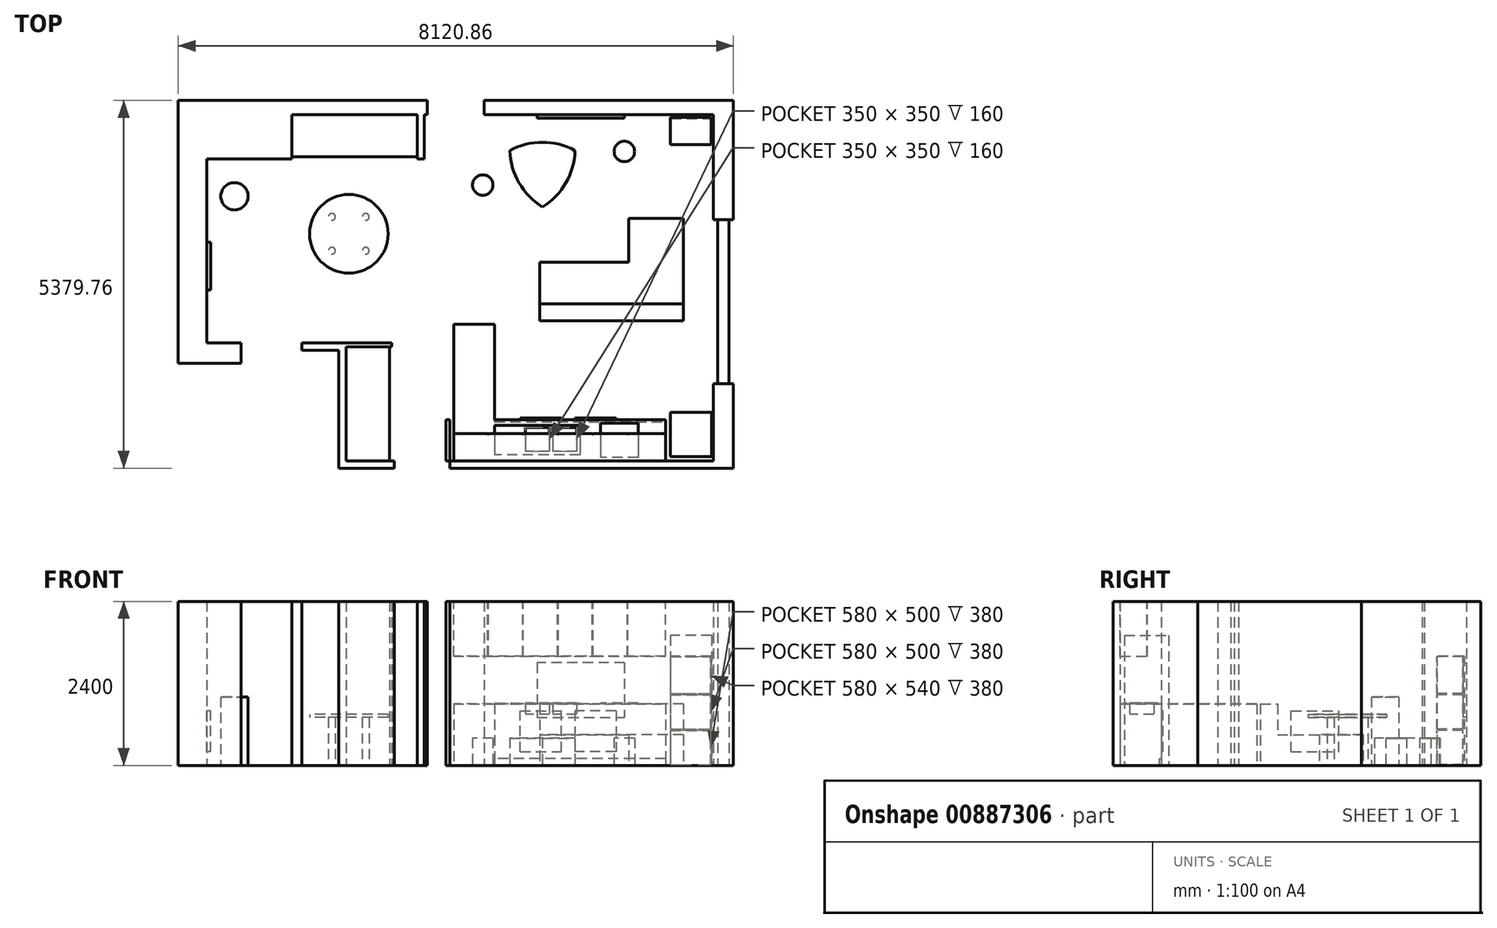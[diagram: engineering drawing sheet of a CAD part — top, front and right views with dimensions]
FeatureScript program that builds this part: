
annotation { "Feature Type Name" : "Feature", "Feature Type Description" : "" }
export const myFeature = defineFeature(function(context is Context, id is Id, definition is map)
    precondition{}
    {
        {
            var Q0;
            Q0=qCreatedBy(makeId("Top.planeOp"),FACE);
            var sketch = newSketch(context, id + "F0", { "sketchPlane" : qUnion([Q0])});
            skLineSegment(sketch, "E0", {"start": v(5332.87, -822.17) * mm, "end": v(1474.75, -822.17) * mm});
            skLineSegment(sketch, "E1", {"start": v(1474.75, -822.17) * mm, "end": v(1474.75, -222.17) * mm});
            skLineSegment(sketch, "E2", {"start": v(1474.75, -222.17) * mm, "end": v(1421.4, -222.17) * mm});
            skLineSegment(sketch, "E3", {"start": v(1421.4, -222.17) * mm, "end": v(1421.4, -822.17) * mm});
            skLineSegment(sketch, "E4", {"start": v(1421.4, -822.17) * mm, "end": v(1474.75, -822.17) * mm});
            skLineSegment(sketch, "E5", {"start": v(5332.87, 309.99) * mm, "end": v(5394.44, 309.99) * mm});
            skLineSegment(sketch, "E6", {"start": v(5394.44, 309.99) * mm, "end": v(5394.44, 2704.75) * mm});
            skLineSegment(sketch, "E7", {"start": v(5394.44, 2704.75) * mm, "end": v(5332.87, 2704.75) * mm});
            skLineSegment(sketch, "E8", {"start": v(5332.87, 2704.75) * mm, "end": v(5332.87, 4243.63) * mm});
            skLineSegment(sketch, "E9", {"start": v(5332.87, 4243.63) * mm, "end": v(1981.19, 4243.63) * mm});
            skLineSegment(sketch, "E10", {"start": v(1981.19, 4243.63) * mm, "end": v(1981.19, 4451) * mm});
            skLineSegment(sketch, "E11", {"start": v(1981.19, 4451) * mm, "end": v(5626.54, 4451) * mm});
            skLineSegment(sketch, "E12", {"start": v(5626.54, 4451) * mm, "end": v(5626.54, 2704.75) * mm});
            skLineSegment(sketch, "E13", {"start": v(5626.54, 2704.75) * mm, "end": v(5394.44, 2704.75) * mm});
            skLineSegment(sketch, "E14", {"start": v(5394.44, 309.99) * mm, "end": v(5626.54, 309.99) * mm});
            skPoint(sketch, "E14.endSnap0", {"position": v(5363.66, 309.99) * mm});
            skLineSegment(sketch, "E15", {"start": v(5626.54, 309.99) * mm, "end": v(5626.54, -928.77) * mm});
            skLineSegment(sketch, "E16", {"start": v(5626.54, -928.77) * mm, "end": v(1474.75, -928.77) * mm});
            skLineSegment(sketch, "E17", {"start": v(1474.75, -928.77) * mm, "end": v(1474.75, -822.17) * mm});
            skLineSegment(sketch, "E18", {"start": v(5558.56, 2704.75) * mm, "end": v(5558.56, 309.99) * mm});
            skLineSegment(sketch, "E19", {"start": v(-37.13, -822.17) * mm, "end": v(664.8, -822.17) * mm});
            skLineSegment(sketch, "E20", {"start": v(664.8, -822.17) * mm, "end": v(664.8, -928.77) * mm});
            skLineSegment(sketch, "E21", {"start": v(664.8, -928.77) * mm, "end": v(-150.57, -928.77) * mm});
            skLineSegment(sketch, "E22", {"start": v(-150.57, -928.77) * mm, "end": v(-150.57, 905.53) * mm});
            skLineSegment(sketch, "E23", {"start": v(-150.57, 905.53) * mm, "end": v(-37.13, 905.53) * mm});
            skLineSegment(sketch, "E24", {"start": v(-37.13, 905.53) * mm, "end": v(-37.13, -26.35) * mm});
            skLineSegment(sketch, "E25", {"start": v(5332.87, 309.99) * mm, "end": v(5332.87, -822.17) * mm});
            skLineSegment(sketch, "E26", {"start": v(-37.13, 905.53) * mm, "end": v(-37.13, -822.17) * mm});
            skLineSegment(sketch, "E27", {"start": v(5332.87, -822.17) * mm, "end": v(1532.87, -822.17) * mm, "construction": true});
            skLineSegment(sketch, "E28", {"start": v(1532.87, -822.17) * mm, "end": v(1532.87, -222.17) * mm});
            skLineSegment(sketch, "E29", {"start": v(1532.87, -222.17) * mm, "end": v(4632.87, -222.17) * mm});
            skLineSegment(sketch, "E30", {"start": v(4894.44, 1227.83) * mm, "end": v(2794.44, 1227.83) * mm});
            skLineSegment(sketch, "E31", {"start": v(2794.44, 1227.83) * mm, "end": v(2794.44, 2087.83) * mm});
            skLineSegment(sketch, "E32", {"start": v(2794.44, 2087.83) * mm, "end": v(4094.44, 2087.83) * mm});
            skLineSegment(sketch, "E33", {"start": v(4894.44, 1227.83) * mm, "end": v(4894.44, 2727.83) * mm});
            skLineSegment(sketch, "E34", {"start": v(4894.44, 2727.83) * mm, "end": v(4094.44, 2727.83) * mm});
            skLineSegment(sketch, "E35", {"start": v(4094.44, 2727.83) * mm, "end": v(4094.44, 2087.83) * mm});
            skLineSegment(sketch, "E36", {"start": v(4894.44, 1227.83) * mm, "end": v(4894.44, 1477.83) * mm, "construction": true});
            skLineSegment(sketch, "E37", {"start": v(4894.44, 1477.83) * mm, "end": v(2794.44, 1477.83) * mm});
            skLineSegment(sketch, "E38.bottom", {"start": v(5301.08, 4208.55) * mm, "end": v(4701.08, 4208.55) * mm});
            skLineSegment(sketch, "E38.top", {"start": v(5301.08, 3808.55) * mm, "end": v(4701.08, 3808.55) * mm});
            skLineSegment(sketch, "E38.left", {"start": v(5301.08, 4208.55) * mm, "end": v(5301.08, 3808.55) * mm});
            skLineSegment(sketch, "E38.right", {"start": v(4701.08, 4208.55) * mm, "end": v(4701.08, 3808.55) * mm});
            skLineSegment(sketch, "E39", {"start": v(4032.87, 4243.63) * mm, "end": v(4032.87, 4193.63) * mm});
            skLineSegment(sketch, "E40", {"start": v(4032.87, 4193.63) * mm, "end": v(2752.87, 4193.63) * mm});
            skLineSegment(sketch, "E41", {"start": v(2752.87, 4193.63) * mm, "end": v(2752.87, 4243.63) * mm});
            skLineSegment(sketch, "E42", {"start": v(2132.87, -302.17) * mm, "end": v(2132.87, -732.17) * mm});
            skLineSegment(sketch, "E43", {"start": v(2132.87, -302.17) * mm, "end": v(3382.87, -302.17) * mm});
            skLineSegment(sketch, "E44", {"start": v(3382.87, -302.17) * mm, "end": v(3382.87, -732.17) * mm});
            skLineSegment(sketch, "E45", {"start": v(3382.87, -732.17) * mm, "end": v(2132.87, -732.17) * mm});
            skLineSegment(sketch, "E46", {"start": v(3382.87, -517.17) * mm, "end": v(3332.87, -517.17) * mm, "construction": true});
            skLineSegment(sketch, "E47", {"start": v(3332.87, -517.17) * mm, "end": v(2982.87, -517.17) * mm, "construction": true});
            skLineSegment(sketch, "E48", {"start": v(2982.87, -517.17) * mm, "end": v(2932.87, -517.17) * mm, "construction": true});
            skLineSegment(sketch, "E49", {"start": v(2932.87, -517.17) * mm, "end": v(2582.87, -517.17) * mm, "construction": true});
            skLineSegment(sketch, "E50.bottom", {"start": v(3332.87, -332.17) * mm, "end": v(2982.87, -332.17) * mm});
            skLineSegment(sketch, "E50.top", {"start": v(3332.87, -682.17) * mm, "end": v(2982.87, -682.17) * mm});
            skLineSegment(sketch, "E50.left", {"start": v(3332.87, -332.17) * mm, "end": v(3332.87, -682.17) * mm});
            skLineSegment(sketch, "E50.right", {"start": v(2982.87, -332.17) * mm, "end": v(2982.87, -682.17) * mm});
            skLineSegment(sketch, "E51.bottom", {"start": v(2932.87, -332.17) * mm, "end": v(2582.87, -332.17) * mm});
            skLineSegment(sketch, "E51.top", {"start": v(2932.87, -682.17) * mm, "end": v(2582.87, -682.17) * mm});
            skLineSegment(sketch, "E51.left", {"start": v(2932.87, -332.17) * mm, "end": v(2932.87, -682.17) * mm});
            skLineSegment(sketch, "E51.right", {"start": v(2582.87, -332.17) * mm, "end": v(2582.87, -682.17) * mm});
            skLineSegment(sketch, "E52.bottom", {"start": v(4232.87, -272.17) * mm, "end": v(3682.87, -272.17) * mm});
            skLineSegment(sketch, "E52.top", {"start": v(4232.87, -772.17) * mm, "end": v(3682.87, -772.17) * mm});
            skLineSegment(sketch, "E52.left", {"start": v(4232.87, -272.17) * mm, "end": v(4232.87, -772.17) * mm});
            skLineSegment(sketch, "E52.right", {"start": v(3682.87, -272.17) * mm, "end": v(3682.87, -772.17) * mm});
            skLineSegment(sketch, "E53", {"start": v(5626.54, 309.99) * mm, "end": v(5626.54, -6920.01) * mm, "construction": true});
            skLineSegment(sketch, "E54", {"start": v(5626.54, -6920.01) * mm, "end": v(109096.54, -6920.01) * mm, "construction": true});
            skLineSegment(sketch, "E55", {"start": v(-150.57, 905.53) * mm, "end": v(-687.76, 905.53) * mm});
            skLineSegment(sketch, "E56", {"start": v(-687.76, 905.53) * mm, "end": v(-687.76, 793.16) * mm});
            skLineSegment(sketch, "E57", {"start": v(-687.76, 793.16) * mm, "end": v(-150.57, 793.16) * mm});
            skLineSegment(sketch, "E58", {"start": v(1145.44, 4243.63) * mm, "end": v(-834.24, 4243.63) * mm});
            skLineSegment(sketch, "E59", {"start": v(-834.24, 4243.63) * mm, "end": v(-834.24, 3594.84) * mm});
            skLineSegment(sketch, "E60", {"start": v(-834.24, 3594.84) * mm, "end": v(-2078.37, 3594.84) * mm});
            skLineSegment(sketch, "E61", {"start": v(-2078.37, 3594.84) * mm, "end": v(-2078.37, 905.53) * mm});
            skLineSegment(sketch, "E62", {"start": v(-2078.37, 905.53) * mm, "end": v(-1579.23, 905.53) * mm});
            skLineSegment(sketch, "E63", {"start": v(-1579.23, 905.53) * mm, "end": v(-1579.23, 605.3) * mm});
            skLineSegment(sketch, "E64", {"start": v(-1579.23, 605.3) * mm, "end": v(-2494.32, 605.3) * mm});
            skLineSegment(sketch, "E65", {"start": v(-2494.32, 605.3) * mm, "end": v(-2494.32, 4451) * mm});
            skLineSegment(sketch, "E66", {"start": v(-2494.32, 4451) * mm, "end": v(1145.44, 4451) * mm});
            skLineSegment(sketch, "E67", {"start": v(1145.44, 4451) * mm, "end": v(1145.44, 4243.63) * mm});
            skLineSegment(sketch, "E68", {"start": v(5332.87, 4243.63) * mm, "end": v(5332.87, 4451) * mm});
            skCircle(sketch, "E69", {"center": v(0, 2500.55) * mm, "radius": 350 * mm, "construction": true});
            skLineSegment(sketch, "E70", {"start": v(-247.49, 2748.03) * mm, "end": v(247.49, 2748.03) * mm, "construction": true});
            skLineSegment(sketch, "E71", {"start": v(247.49, 2748.03) * mm, "end": v(247.49, 2253.06) * mm, "construction": true});
            skLineSegment(sketch, "E72", {"start": v(247.49, 2253.06) * mm, "end": v(-247.49, 2253.06) * mm, "construction": true});
            skCircle(sketch, "E73", {"center": v(-247.49, 2748.03) * mm, "radius": 50 * mm});
            skCircle(sketch, "E74", {"center": v(247.49, 2748.03) * mm, "radius": 50 * mm});
            skCircle(sketch, "E75", {"center": v(247.49, 2253.06) * mm, "radius": 50 * mm});
            skCircle(sketch, "E76", {"center": v(-247.49, 2253.06) * mm, "radius": 50 * mm});
            skCircle(sketch, "E77", {"center": v(0, 2500.55) * mm, "radius": 575 * mm});
            skCircle(sketch, "E78", {"center": v(2832.87, 3443.63) * mm, "radius": 550 * mm, "construction": true});
            skLineSegment(sketch, "E79", {"start": v(2832.87, 3443.63) * mm, "end": v(2832.87, 2893.63) * mm, "construction": true});
            skArc(sketch, "E80", {"start": v(2832.87, 2893.63) * mm, "mid": v(3175.58, 3245.77) * mm, "end": v(3309.19, 3718.63) * mm});
            skArc(sketch, "E81", {"start": v(3309.19, 3718.63) * mm, "mid": v(2832.87, 3839.36) * mm, "end": v(2356.56, 3718.63) * mm});
            skArc(sketch, "E82", {"start": v(2356.56, 3718.63) * mm, "mid": v(2490.17, 3245.77) * mm, "end": v(2832.87, 2893.63) * mm});
            skLineSegment(sketch, "E83", {"start": v(2832.87, 3443.63) * mm, "end": v(3309.19, 3718.63) * mm, "construction": true});
            skLineSegment(sketch, "E84", {"start": v(2832.87, 3443.63) * mm, "end": v(2356.56, 3718.63) * mm, "construction": true});
            skLineSegment(sketch, "E85", {"start": v(3309.19, 3718.63) * mm, "end": v(2356.56, 3718.63) * mm, "construction": true});
            skLineSegment(sketch, "E86", {"start": v(2356.56, 3718.63) * mm, "end": v(2832.87, 2893.63) * mm, "construction": true});
            skLineSegment(sketch, "E87", {"start": v(2832.87, 2893.63) * mm, "end": v(3309.19, 3718.63) * mm, "construction": true});
            skCircle(sketch, "E88", {"center": v(4030.54, 3705.1) * mm, "radius": 150 * mm});
            skCircle(sketch, "E89", {"center": v(1959.1, 3213.96) * mm, "radius": 150 * mm});
            skLineSegment(sketch, "E90", {"start": v(1101.26, 4243.63) * mm, "end": v(1101.26, 3594.84) * mm});
            skLineSegment(sketch, "E91", {"start": v(1101.26, 3594.84) * mm, "end": v(1001.26, 3594.84) * mm});
            skLineSegment(sketch, "E92", {"start": v(1001.26, 3594.84) * mm, "end": v(1001.26, 4243.63) * mm});
            skLineSegment(sketch, "E93", {"start": v(1001.26, 3627.05) * mm, "end": v(-834.24, 3627.05) * mm});
            skLineSegment(sketch, "E94", {"start": v(597.97, -822.17) * mm, "end": v(597.97, 845.53) * mm});
            skLineSegment(sketch, "E95", {"start": v(597.97, 905.53) * mm, "end": v(624.1, 905.53) * mm});
            skLineSegment(sketch, "E96", {"start": v(624.1, 905.53) * mm, "end": v(624.1, 845.53) * mm});
            skLineSegment(sketch, "E97", {"start": v(624.1, 845.53) * mm, "end": v(-37.13, 845.53) * mm});
            skLineSegment(sketch, "E98", {"start": v(-37.13, 905.53) * mm, "end": v(597.97, 905.53) * mm});
            skCircle(sketch, "E99", {"center": v(-1673.98, 3049.9) * mm, "radius": 200 * mm});
            skLineSegment(sketch, "E100", {"start": v(1532.87, -222.17) * mm, "end": v(1532.87, 1177.83) * mm});
            skLineSegment(sketch, "E101", {"start": v(1532.87, 1177.83) * mm, "end": v(2132.87, 1177.83) * mm});
            skLineSegment(sketch, "E102", {"start": v(2132.87, 1177.83) * mm, "end": v(2132.87, -222.17) * mm});
            skLineSegment(sketch, "E103", {"start": v(4632.87, -222.17) * mm, "end": v(4632.87, -822.17) * mm});
            skLineSegment(sketch, "E104.bottom", {"start": v(5306, -761.63) * mm, "end": v(4706, -761.63) * mm});
            skLineSegment(sketch, "E104.top", {"start": v(5306, -111.63) * mm, "end": v(4706, -111.63) * mm});
            skLineSegment(sketch, "E104.left", {"start": v(5306, -761.63) * mm, "end": v(5306, -111.63) * mm});
            skLineSegment(sketch, "E104.right", {"start": v(4706, -761.63) * mm, "end": v(4706, -111.63) * mm});
            skSolve(sketch);
        }
        {
            var Q0;
            {var subQ0=sQuery(id+"F0.wireOp",EDGE,"E7");Q0=makeQuery(id+"F0.imprint","IMPRINT",FACE,{"disambiguationData":[TD([[makeQuery(id+"F0.imprint","IMPRINT",EDGE,{"derivedFrom":subQ0}),-1.0]])]});}
            var Q1;
            Q1=makeQuery(id+"F0.imprint","IMPRINT",FACE,{"disambiguationData":[TD([[makeQuery(id+"F0.imprint","IMPRINT",EDGE,{"derivedFrom":sQuery(id+"F0.wireOp",EDGE,"E0")}),1.0]])]});
            var Q2;
            {var subQ0=sQuery(id+"F0.wireOp",EDGE,"E19");Q2=makeQuery(id+"F0.imprint","IMPRINT",FACE,{"disambiguationData":[TD([[makeQuery(id+"F0.imprint","IMPRINT",EDGE,{"derivedFrom":subQ0}),-1.0]])]});}
            var Q3;
            Q3=makeQuery(id+"F0.imprint","IMPRINT",FACE,{"disambiguationData":[TD([[makeQuery(id+"F0.imprint","IMPRINT",EDGE,{"derivedFrom":sQuery(id+"F0.wireOp",EDGE,"E1")}),1.0]])]});
            var Q4;
            Q4=makeQuery(id+"F0.imprint","IMPRINT",FACE,{"disambiguationData":[TD([[makeQuery(id+"F0.imprint","IMPRINT",EDGE,{"derivedFrom":sQuery(id+"F0.wireOp",EDGE,"E58")}),-1.0]])]});
            var Q5;
            {var subQ0=sQuery(id+"F0.wireOp",EDGE,"E55");Q5=makeQuery(id+"F0.imprint","IMPRINT",FACE,{"disambiguationData":[TD([[makeQuery(id+"F0.imprint","IMPRINT",EDGE,{"derivedFrom":subQ0}),1.0]])]});}
            var Q6;
            {var subQ0=sQuery(id+"F0.wireOp",EDGE,"E10");Q6=makeQuery(id+"F0.imprint","IMPRINT",FACE,{"disambiguationData":[TD([[makeQuery(id+"F0.imprint","IMPRINT",EDGE,{"derivedFrom":subQ0}),-1.0]])]});}
            var Q7;
            {var subQ3=sQuery(id+"F0.wireOp",EDGE,"E90");Q7=makeQuery(id+"F0.imprint","IMPRINT",FACE,{"disambiguationData":[TD([[makeQuery(id+"F0.imprint","IMPRINT",EDGE,{"derivedFrom":subQ3}),-1.0]])]});}
            var Q8;
            Q8=makeQuery(id+"F0.imprint","IMPRINT",FACE,{"disambiguationData":[TD([[makeQuery(id+"F0.imprint","IMPRINT",EDGE,{"derivedFrom":sQuery(id+"F0.wireOp",EDGE,"E95")}),-1.0]])]});
            extrude(context, id + "F1", {"entities" : qUnion([Q0, Q1, Q2, Q3, Q4, Q5, Q6, Q7, Q8]), "depth" : 2400 * mm, "offsetDistance" : 25 * mm});
        }
        {
            var Q0;
            {var subQ1=sQuery(id+"F0.wireOp",EDGE,"E28");Q0=makeQuery(id+"F0.imprint","IMPRINT",FACE,{"disambiguationData":[TD([[makeQuery(id+"F0.imprint","IMPRINT",EDGE,{"derivedFrom":subQ1}),-1.0]])]});}
            var Q1;
            {var subQ0=sQuery(id+"F0.wireOp",EDGE,"E100");Q1=makeQuery(id+"F0.imprint","IMPRINT",FACE,{"disambiguationData":[TD([[makeQuery(id+"F0.imprint","IMPRINT",EDGE,{"derivedFrom":subQ0}),-1.0]])]});}
            extrude(context, id + "F2", {"entities" : qUnion([Q0, Q1]), "depth" : 900 * mm, "offsetDistance" : 25 * mm});
        }
        {
            var Q0;
            Q0=makeQuery(id+"F1.opExtrude","CAP_FACE",FACE,{"disambiguationData":[OSD([sQuery(id+"F0.wireOp",EDGE,"E0"),sQuery(id+"F0.wireOp",EDGE,"E5"),sQuery(id+"F0.wireOp",EDGE,"E14"),sQuery(id+"F0.wireOp",EDGE,"E15"),sQuery(id+"F0.wireOp",EDGE,"E16"),sQuery(id+"F0.wireOp",EDGE,"E17"),sQuery(id+"F0.wireOp",EDGE,"E25")])],"isStart":false});
            var sketch = newSketch(context, id + "F3", { "sketchPlane" : qUnion([Q0])});
            skLineSegment(sketch, "E105", {"start": v(4632.87, -822.17) * mm, "end": v(1532.87, -822.17) * mm});
            skLineSegment(sketch, "E106", {"start": v(1532.87, -822.17) * mm, "end": v(1532.87, -422.17) * mm});
            skLineSegment(sketch, "E107", {"start": v(1532.87, -422.17) * mm, "end": v(4632.87, -422.17) * mm});
            skLineSegment(sketch, "E108", {"start": v(4632.87, -822.17) * mm, "end": v(4632.87, -422.17) * mm});
            skSolve(sketch);
        }
        {
            var Q0;
            Q0=makeQuery(id+"F3.imprint","IMPRINT",FACE,{"disambiguationData":[TD([[makeQuery(id+"F3.imprint","IMPRINT",EDGE,{"derivedFrom":sQuery(id+"F3.wireOp",EDGE,"E105")}),-1.0]])]});
            extrude(context, id + "F4", {"entities" : qUnion([Q0]), "oppositeDirection" : true, "depth" : 800 * mm, "offsetDistance" : 25 * mm});
        }
        {
            var Q0;
            Q0=makeQuery(id+"F0.imprint","IMPRINT",FACE,{"disambiguationData":[TD([[makeQuery(id+"F0.imprint","IMPRINT",EDGE,{"derivedFrom":sQuery(id+"F0.wireOp",EDGE,"nRFYV91U-GxAd-OucP-NhtY-qvlqKsGYWcc8.bottom")}),1.0]])]});
            var Q1;
            Q1=makeQuery(id+"F0.imprint","IMPRINT",FACE,{"disambiguationData":[TD([[makeQuery(id+"F0.imprint","IMPRINT",EDGE,{"derivedFrom":sQuery(id+"F0.wireOp",EDGE,"E104.bottom")}),-1.0]])]});
            extrude(context, id + "F5", {"entities" : qUnion([Q0, Q1]), "depth" : 1900 * mm, "offsetDistance" : 25 * mm});
        }
        {
            var Q0;
            {var subQ0=sQuery(id+"F0.wireOp",EDGE,"E30");Q0=makeQuery(id+"F0.imprint","IMPRINT",FACE,{"disambiguationData":[TD([[makeQuery(id+"F0.imprint","IMPRINT",EDGE,{"derivedFrom":subQ0}),-1.0]])]});}
            extrude(context, id + "F6", {"entities" : qUnion([Q0]), "depth" : 900 * mm, "offsetDistance" : 25 * mm});
        }
        {
            var Q0;
            {var subQ3=sQuery(id+"F0.wireOp",EDGE,"E32");Q0=makeQuery(id+"F0.imprint","IMPRINT",FACE,{"disambiguationData":[TD([[makeQuery(id+"F0.imprint","IMPRINT",EDGE,{"derivedFrom":subQ3}),-1.0]])]});}
            extrude(context, id + "F7", {"entities" : qUnion([Q0]), "operationType" : NewBodyOperationType.ADD, "depth" : 450 * mm, "offsetDistance" : 25 * mm});
        }
        {
            var Q0;
            Q0=makeQuery(id+"F0.imprint","IMPRINT",FACE,{"disambiguationData":[TD([[makeQuery(id+"F0.imprint","IMPRINT",EDGE,{"derivedFrom":sQuery(id+"F0.wireOp",EDGE,"E42")}),1.0]])]});
            extrude(context, id + "F8", {"entities" : qUnion([Q0]), "operationType" : NewBodyOperationType.ADD, "depth" : 910 * mm, "offsetDistance" : 25 * mm});
        }
        {
            var Q0;
            Q0=makeQuery(id+"F0.imprint","IMPRINT",FACE,{"disambiguationData":[TD([[makeQuery(id+"F0.imprint","IMPRINT",EDGE,{"derivedFrom":sQuery(id+"F0.wireOp",EDGE,"E50.bottom")}),1.0]])]});
            var Q1;
            Q1=makeQuery(id+"F0.imprint","IMPRINT",FACE,{"disambiguationData":[TD([[makeQuery(id+"F0.imprint","IMPRINT",EDGE,{"derivedFrom":sQuery(id+"F0.wireOp",EDGE,"E51.bottom")}),1.0]])]});
            extrude(context, id + "F9", {"entities" : qUnion([Q0, Q1]), "operationType" : NewBodyOperationType.ADD, "depth" : 750 * mm, "offsetDistance" : 25 * mm});
        }
        {
            var Q0;
            Q0=makeQuery(id+"F0.imprint","IMPRINT",FACE,{"disambiguationData":[TD([[makeQuery(id+"F0.imprint","IMPRINT",EDGE,{"derivedFrom":sQuery(id+"F0.wireOp",EDGE,"E52.bottom")}),1.0]])]});
            extrude(context, id + "F10", {"entities" : qUnion([Q0]), "operationType" : NewBodyOperationType.ADD, "depth" : 910 * mm, "offsetDistance" : 25 * mm});
        }
        {
            var Q0;
            {var subQ0=sQuery(id+"F0.wireOp",EDGE,"E6");Q0=makeQuery(id+"F0.imprint","IMPRINT",FACE,{"disambiguationData":[TD([[makeQuery(id+"F0.imprint","IMPRINT",EDGE,{"derivedFrom":subQ0}),-1.0]])]});}
            extrude(context, id + "F11", {"entities" : qUnion([Q0]), "depth" : 2400 * mm, "offsetDistance" : 25 * mm});
        }
        {
            var Q0;
            Q0=makeQuery(id+"F0.imprint","IMPRINT",FACE,{"disambiguationData":[TD([[makeQuery(id+"F0.imprint","IMPRINT",EDGE,{"derivedFrom":sQuery(id+"F0.wireOp",EDGE,"E73")}),-1.0]])]});
            var Q1;
            Q1=makeQuery(id+"Fm7Inrb7nq87sZd_8.opExtrude","CAP_FACE",FACE,{"disambiguationData":[OSD([sQuery(id+"F0.wireOp",EDGE,"E74")])],"isStart":false});
            var Q2;
            Q2=makeQuery(id+"Fm7Inrb7nq87sZd_8.opExtrude","CAP_FACE",FACE,{"disambiguationData":[OSD([sQuery(id+"F0.wireOp",EDGE,"E75")])],"isStart":false});
            var Q3;
            Q3=makeQuery(id+"Fm7Inrb7nq87sZd_8.opExtrude","CAP_FACE",FACE,{"disambiguationData":[OSD([sQuery(id+"F0.wireOp",EDGE,"E73")])],"isStart":false});
            var Q4;
            Q4=makeQuery(id+"Fm7Inrb7nq87sZd_8.opExtrude","CAP_FACE",FACE,{"disambiguationData":[OSD([sQuery(id+"F0.wireOp",EDGE,"E76")])],"isStart":false});
            var Q5;
            Q5=makeQuery(id+"F0.imprint","IMPRINT",FACE,{"disambiguationData":[TD([[makeQuery(id+"F0.imprint","IMPRINT",EDGE,{"derivedFrom":sQuery(id+"F0.wireOp",EDGE,"E74")}),1.0]])]});
            var Q6;
            Q6=makeQuery(id+"F0.imprint","IMPRINT",FACE,{"disambiguationData":[TD([[makeQuery(id+"F0.imprint","IMPRINT",EDGE,{"derivedFrom":sQuery(id+"F0.wireOp",EDGE,"E75")}),1.0]])]});
            var Q7;
            Q7=makeQuery(id+"F0.imprint","IMPRINT",FACE,{"disambiguationData":[TD([[makeQuery(id+"F0.imprint","IMPRINT",EDGE,{"derivedFrom":sQuery(id+"F0.wireOp",EDGE,"E73")}),1.0]])]});
            var Q8;
            Q8=makeQuery(id+"F0.imprint","IMPRINT",FACE,{"disambiguationData":[TD([[makeQuery(id+"F0.imprint","IMPRINT",EDGE,{"derivedFrom":sQuery(id+"F0.wireOp",EDGE,"E76")}),1.0]])]});
            extrude(context, id + "F12", {"entities" : qUnion([Q0, Q1, Q2, Q3, Q4, Q5, Q6, Q7, Q8]), "depth" : 750 * mm, "offsetDistance" : 25 * mm});
        }
        {
            var Q0;
            Q0=makeQuery(id+"F0.imprint","IMPRINT",FACE,{"disambiguationData":[TD([[makeQuery(id+"F0.imprint","IMPRINT",EDGE,{"derivedFrom":sQuery(id+"F0.wireOp",EDGE,"E73")}),-1.0]])]});
            extrude(context, id + "F13", {"entities" : qUnion([Q0]), "depth" : 700 * mm, "offsetDistance" : 25 * mm});
        }
        {
            var Q0;
            Q0=makeQuery(id+"F13.opExtrude","SWEPT_BODY",BODY,{"disambiguationData":[OSD([sQuery(id+"F0.wireOp",EDGE,"E73"),sQuery(id+"F0.wireOp",EDGE,"E74"),sQuery(id+"F0.wireOp",EDGE,"E75"),sQuery(id+"F0.wireOp",EDGE,"E76"),sQuery(id+"F0.wireOp",EDGE,"E77")])]});
            var Q1;
            Q1=makeQuery(id+"F12.opExtrude","SWEPT_BODY",BODY,{"disambiguationData":[OSD([sQuery(id+"F0.wireOp",EDGE,"E73"),sQuery(id+"F0.wireOp",EDGE,"E74"),sQuery(id+"F0.wireOp",EDGE,"E75"),sQuery(id+"F0.wireOp",EDGE,"E76"),sQuery(id+"F0.wireOp",EDGE,"E77")])]});
            booleanBodies(context, id + "F14", {"operationType" : BooleanOperationType.SUBTRACTION, "tools" : qUnion([Q0]), "targets" : qUnion([Q1])});
        }
        {
            var Q0;
            {var subQ0=sQuery(id+"F0.wireOp",EDGE,"E39");Q0=makeQuery(id+"F0.imprint","IMPRINT",FACE,{"disambiguationData":[TD([[makeQuery(id+"F0.imprint","IMPRINT",EDGE,{"derivedFrom":subQ0}),-1.0]])]});}
            extrude(context, id + "F15", {"entities" : qUnion([Q0]), "depth" : 1500 * mm, "offsetDistance" : 25 * mm});
        }
        {
            var Q0;
            Q0=makeQuery(id+"F15.opExtrude","SWEPT_FACE",FACE,{"disambiguationData":[OSD([sQuery(id+"F0.wireOp",EDGE,"E40")])]});
            var sketch = newSketch(context, id + "F16", { "sketchPlane" : qUnion([Q0])});
            skLineSegment(sketch, "E109.bottom", {"start": v(2752.87, 0) * mm, "end": v(4032.87, 0) * mm});
            skLineSegment(sketch, "E109.top", {"start": v(2752.87, 700) * mm, "end": v(4032.87, 700) * mm});
            skLineSegment(sketch, "E109.left", {"start": v(2752.87, 0) * mm, "end": v(2752.87, 700) * mm});
            skLineSegment(sketch, "E109.right", {"start": v(4032.87, 0) * mm, "end": v(4032.87, 700) * mm});
            skSolve(sketch);
        }
        {
            var Q0;
            Q0=makeQuery(id+"F16.imprint","IMPRINT",FACE,{"disambiguationData":[TD([[makeQuery(id+"F16.imprint","IMPRINT",EDGE,{"derivedFrom":sQuery(id+"F16.wireOp",EDGE,"E109.bottom")}),-1.0]])]});
            extrude(context, id + "F17", {"entities" : qUnion([Q0]), "operationType" : NewBodyOperationType.REMOVE, "oppositeDirection" : true, "depth" : 50 * mm, "offsetDistance" : 25 * mm});
        }
        {
            var Q0;
            Q0=makeQuery(id+"F0.imprint","IMPRINT",FACE,{"disambiguationData":[TD([[makeQuery(id+"F0.imprint","IMPRINT",EDGE,{"derivedFrom":sQuery(id+"F0.wireOp",EDGE,"E80")}),1.0]])]});
            var Q1;
            Q1=makeQuery(id+"F0.imprint","IMPRINT",FACE,{"disambiguationData":[TD([[makeQuery(id+"F0.imprint","IMPRINT",EDGE,{"derivedFrom":sQuery(id+"F0.wireOp",EDGE,"E88")}),1.0]])]});
            var Q2;
            Q2=makeQuery(id+"F0.imprint","IMPRINT",FACE,{"disambiguationData":[TD([[makeQuery(id+"F0.imprint","IMPRINT",EDGE,{"derivedFrom":sQuery(id+"F0.wireOp",EDGE,"E89")}),1.0]])]});
            extrude(context, id + "F18", {"entities" : qUnion([Q0, Q1, Q2]), "depth" : 400 * mm, "offsetDistance" : 25 * mm});
        }
        {
            var Q0;
            Q0=makeQuery(id+"F0.imprint","IMPRINT",FACE,{"disambiguationData":[TD([[makeQuery(id+"F0.imprint","IMPRINT",EDGE,{"derivedFrom":sQuery(id+"F0.wireOp",EDGE,"E38.bottom")}),1.0]])]});
            extrude(context, id + "F19", {"entities" : qUnion([Q0]), "depth" : 1600 * mm, "offsetDistance" : 25 * mm});
        }
        {
            var Q0;
            Q0=makeQuery(id+"F19.opExtrude","SWEPT_FACE",FACE,{"disambiguationData":[OSD([sQuery(id+"F0.wireOp",EDGE,"E38.top")])]});
            var sketch = newSketch(context, id + "F20", { "sketchPlane" : qUnion([Q0])});
            skCircle(sketch, "E110", {"center": v(4701.08, 1600) * mm, "radius": 10 * mm, "construction": true});
            skCircle(sketch, "E111", {"center": v(5301.08, 1600) * mm, "radius": 10 * mm, "construction": true});
            skLineSegment(sketch, "E112", {"start": v(4701.08, 1590) * mm, "end": v(5301.08, 1590) * mm, "construction": true});
            skCircle(sketch, "E113", {"center": v(4701.08, 0) * mm, "radius": 10 * mm, "construction": true});
            skCircle(sketch, "E114", {"center": v(5301.08, 0) * mm, "radius": 10 * mm, "construction": true});
            skLineSegment(sketch, "E115", {"start": v(5301.08, 10) * mm, "end": v(4701.08, 10) * mm, "construction": true});
            skLineSegment(sketch, "E116", {"start": v(4711.08, 0) * mm, "end": v(4711.08, 10) * mm, "construction": true});
            skLineSegment(sketch, "E117", {"start": v(5291.08, 0) * mm, "end": v(5291.08, 10) * mm, "construction": true});
            skLineSegment(sketch, "E118", {"start": v(4711.08, 1600) * mm, "end": v(4711.08, 1590) * mm, "construction": true});
            skLineSegment(sketch, "E119.bottom", {"start": v(4711.08, 1590) * mm, "end": v(5291.08, 1590) * mm, "construction": true});
            skLineSegment(sketch, "E119.top", {"start": v(4711.08, 10) * mm, "end": v(5291.08, 10) * mm, "construction": true});
            skLineSegment(sketch, "E119.left", {"start": v(4711.08, 1590) * mm, "end": v(4711.08, 10) * mm, "construction": true});
            skLineSegment(sketch, "E119.right", {"start": v(5291.08, 1590) * mm, "end": v(5291.08, 10) * mm, "construction": true});
            skLineSegment(sketch, "E120.bottom", {"start": v(4711.08, 10) * mm, "end": v(5291.08, 10) * mm});
            skLineSegment(sketch, "E120.top", {"start": v(4711.08, 510) * mm, "end": v(5291.08, 510) * mm});
            skLineSegment(sketch, "E120.left", {"start": v(4711.08, 10) * mm, "end": v(4711.08, 510) * mm});
            skLineSegment(sketch, "E120.right", {"start": v(5291.08, 10) * mm, "end": v(5291.08, 510) * mm});
            skLineSegment(sketch, "E121", {"start": v(4711.08, 510) * mm, "end": v(4711.08, 530) * mm, "construction": true});
            skLineSegment(sketch, "E122.bottom", {"start": v(4711.08, 530) * mm, "end": v(5291.08, 530) * mm});
            skLineSegment(sketch, "E122.top", {"start": v(4711.08, 1030) * mm, "end": v(5291.08, 1030) * mm});
            skLineSegment(sketch, "E122.left", {"start": v(4711.08, 530) * mm, "end": v(4711.08, 1030) * mm});
            skLineSegment(sketch, "E122.right", {"start": v(5291.08, 530) * mm, "end": v(5291.08, 1030) * mm});
            skLineSegment(sketch, "E123", {"start": v(4711.08, 1030) * mm, "end": v(4711.08, 1050) * mm, "construction": true});
            skLineSegment(sketch, "E124.bottom", {"start": v(4711.08, 1050) * mm, "end": v(5291.08, 1050) * mm});
            skLineSegment(sketch, "E124.top", {"start": v(4711.08, 1590) * mm, "end": v(5291.08, 1590) * mm});
            skLineSegment(sketch, "E124.left", {"start": v(4711.08, 1050) * mm, "end": v(4711.08, 1590) * mm});
            skLineSegment(sketch, "E124.right", {"start": v(5291.08, 1050) * mm, "end": v(5291.08, 1590) * mm});
            skSolve(sketch);
        }
        {
            var Q0;
            Q0=makeQuery(id+"F20.imprint","IMPRINT",FACE,{"disambiguationData":[TD([[makeQuery(id+"F20.imprint","IMPRINT",EDGE,{"derivedFrom":sQuery(id+"F20.wireOp",EDGE,"E124.bottom")}),1.0]])]});
            var Q1;
            Q1=makeQuery(id+"F20.imprint","IMPRINT",FACE,{"disambiguationData":[TD([[makeQuery(id+"F20.imprint","IMPRINT",EDGE,{"derivedFrom":sQuery(id+"F20.wireOp",EDGE,"E122.bottom")}),1.0]])]});
            var Q2;
            Q2=makeQuery(id+"F20.imprint","IMPRINT",FACE,{"disambiguationData":[TD([[makeQuery(id+"F20.imprint","IMPRINT",EDGE,{"derivedFrom":sQuery(id+"F20.wireOp",EDGE,"E120.bottom")}),1.0]])]});
            extrude(context, id + "F21", {"entities" : qUnion([Q0, Q1, Q2]), "operationType" : NewBodyOperationType.REMOVE, "oppositeDirection" : true, "depth" : 380 * mm, "offsetDistance" : 25 * mm});
        }
        {
            var Q0;
            Q0=makeQuery(id+"F2.opExtrude","SWEPT_FACE",FACE,{"disambiguationData":[OSD([sQuery(id+"F0.wireOp",EDGE,"E29")])]});
            var sketch = newSketch(context, id + "F22", { "sketchPlane" : qUnion([Q0])});
            skLineSegment(sketch, "E125", {"start": v(-4632.87, 100) * mm, "end": v(-4632.87, 100) * mm});
            skLineSegment(sketch, "E126.bottom", {"start": v(-2507.98, 200) * mm, "end": v(-3107.98, 200) * mm});
            skLineSegment(sketch, "E126.top", {"start": v(-2507.98, 800) * mm, "end": v(-3107.98, 800) * mm});
            skLineSegment(sketch, "E126.left", {"start": v(-2507.98, 200) * mm, "end": v(-2507.98, 800) * mm});
            skLineSegment(sketch, "E126.right", {"start": v(-3107.98, 200) * mm, "end": v(-3107.98, 800) * mm});
            skLineSegment(sketch, "E127", {"start": v(-1532.87, 900) * mm, "end": v(-1532.87, 0) * mm, "construction": true});
            skLineSegment(sketch, "E128", {"start": v(-4632.87, 900) * mm, "end": v(-4632.87, 0) * mm, "construction": true});
            skLineSegment(sketch, "E129.bottom", {"start": v(-3907.98, 800) * mm, "end": v(-3307.98, 800) * mm});
            skLineSegment(sketch, "E129.top", {"start": v(-3907.98, 200) * mm, "end": v(-3307.98, 200) * mm});
            skLineSegment(sketch, "E129.left", {"start": v(-3907.98, 800) * mm, "end": v(-3907.98, 200) * mm});
            skLineSegment(sketch, "E129.right", {"start": v(-3307.98, 800) * mm, "end": v(-3307.98, 200) * mm});
            skLineSegment(sketch, "E130", {"start": v(-4632.87, 100) * mm, "end": v(-2132.87, 100) * mm});
            skSolve(sketch);
        }
        {
            var Q0;
            Q0=makeQuery(id+"F22.imprint","IMPRINT",FACE,{"disambiguationData":[TD([[makeQuery(id+"F22.imprint","IMPRINT",EDGE,{"derivedFrom":sQuery(id+"F22.wireOp",EDGE,"E129.bottom")}),-1.0]])]});
            var Q1;
            Q1=makeQuery(id+"F22.imprint","IMPRINT",FACE,{"disambiguationData":[TD([[makeQuery(id+"F22.imprint","IMPRINT",EDGE,{"derivedFrom":sQuery(id+"F22.wireOp",EDGE,"E126.bottom")}),-1.0]])]});
            extrude(context, id + "F23", {"entities" : qUnion([Q0, Q1]), "operationType" : NewBodyOperationType.ADD, "depth" : 25 * mm, "offsetDistance" : 25 * mm});
        }
        {
            var Q0;
            {var subQ0=sQuery(id+"F22.wireOp",EDGE,"E130");Q0=makeQuery(id+"F22.imprint","IMPRINT",FACE,{"disambiguationData":[TD([[makeQuery(id+"F22.imprint","IMPRINT",EDGE,{"derivedFrom":subQ0}),-1.0]])]});}
            extrude(context, id + "F24", {"entities" : qUnion([Q0]), "operationType" : NewBodyOperationType.REMOVE, "oppositeDirection" : true, "depth" : 30 * mm, "offsetDistance" : 25 * mm});
        }
        {
            var Q0;
            Q0=makeQuery(id+"F4.opExtrude","SWEPT_FACE",FACE,{"disambiguationData":[OSD([sQuery(id+"F3.wireOp",EDGE,"E107")])]});
            var sketch = newSketch(context, id + "F25", { "sketchPlane" : qUnion([Q0])});
            skLineSegment(sketch, "E131", {"start": v(-1532.87, 1600) * mm, "end": v(-1532.87, 2400) * mm, "construction": true});
            skLineSegment(sketch, "E132", {"start": v(-1532.87, 1600) * mm, "end": v(-2032.87, 1600) * mm, "construction": true});
            skLineSegment(sketch, "E133.bottom", {"start": v(-2032.87, 1600) * mm, "end": v(-2042.87, 1600) * mm});
            skLineSegment(sketch, "E133.top", {"start": v(-2032.87, 2400) * mm, "end": v(-2042.87, 2400) * mm});
            skLineSegment(sketch, "E133.left", {"start": v(-2032.87, 1600) * mm, "end": v(-2032.87, 2400) * mm});
            skLineSegment(sketch, "E133.right", {"start": v(-2042.87, 1600) * mm, "end": v(-2042.87, 2400) * mm});
            skLineSegment(sketch, "E134", {"start": v(-2042.87, 1600) * mm, "end": v(-2542.87, 1600) * mm, "construction": true});
            skLineSegment(sketch, "E135", {"start": v(-2542.87, 1600) * mm, "end": v(-3052.87, 1600) * mm, "construction": true});
            skLineSegment(sketch, "E136", {"start": v(-3052.87, 1600) * mm, "end": v(-3562.87, 1600) * mm, "construction": true});
            skLineSegment(sketch, "E137", {"start": v(-3562.87, 1600) * mm, "end": v(-4072.87, 1600) * mm, "construction": true});
            skLineSegment(sketch, "E138.bottom", {"start": v(-2542.87, 1600) * mm, "end": v(-2552.87, 1600) * mm});
            skLineSegment(sketch, "E138.top", {"start": v(-2542.87, 2400) * mm, "end": v(-2552.87, 2400) * mm});
            skLineSegment(sketch, "E138.left", {"start": v(-2542.87, 1600) * mm, "end": v(-2542.87, 2400) * mm});
            skLineSegment(sketch, "E138.right", {"start": v(-2552.87, 1600) * mm, "end": v(-2552.87, 2400) * mm});
            skLineSegment(sketch, "E139.bottom", {"start": v(-3052.87, 1600) * mm, "end": v(-3062.87, 1600) * mm});
            skLineSegment(sketch, "E139.top", {"start": v(-3052.87, 2400) * mm, "end": v(-3062.87, 2400) * mm});
            skLineSegment(sketch, "E139.left", {"start": v(-3052.87, 1600) * mm, "end": v(-3052.87, 2400) * mm});
            skLineSegment(sketch, "E139.right", {"start": v(-3062.87, 1600) * mm, "end": v(-3062.87, 2400) * mm});
            skLineSegment(sketch, "E140.bottom", {"start": v(-3562.87, 1600) * mm, "end": v(-3572.87, 1600) * mm});
            skLineSegment(sketch, "E140.top", {"start": v(-3562.87, 2400) * mm, "end": v(-3572.87, 2400) * mm});
            skLineSegment(sketch, "E140.left", {"start": v(-3562.87, 1600) * mm, "end": v(-3562.87, 2400) * mm});
            skLineSegment(sketch, "E140.right", {"start": v(-3572.87, 1600) * mm, "end": v(-3572.87, 2400) * mm});
            skLineSegment(sketch, "E141.bottom", {"start": v(-4072.87, 1600) * mm, "end": v(-4082.87, 1600) * mm});
            skLineSegment(sketch, "E141.top", {"start": v(-4072.87, 2400) * mm, "end": v(-4082.87, 2400) * mm});
            skLineSegment(sketch, "E141.left", {"start": v(-4072.87, 1600) * mm, "end": v(-4072.87, 2400) * mm});
            skLineSegment(sketch, "E141.right", {"start": v(-4082.87, 1600) * mm, "end": v(-4082.87, 2400) * mm});
            skLineSegment(sketch, "E142", {"start": v(-4082.87, 1600) * mm, "end": v(-5282.87, 1600) * mm, "construction": true});
            skSolve(sketch);
        }
        {
            var Q0;
            Q0=makeQuery(id+"F25.imprint","IMPRINT",FACE,{"disambiguationData":[TD([[makeQuery(id+"F25.imprint","IMPRINT",EDGE,{"derivedFrom":sQuery(id+"F25.wireOp",EDGE,"E133.bottom")}),-1.0]])]});
            var Q1;
            Q1=makeQuery(id+"F25.imprint","IMPRINT",FACE,{"disambiguationData":[TD([[makeQuery(id+"F25.imprint","IMPRINT",EDGE,{"derivedFrom":sQuery(id+"F25.wireOp",EDGE,"E138.bottom")}),-1.0]])]});
            var Q2;
            Q2=makeQuery(id+"F25.imprint","IMPRINT",FACE,{"disambiguationData":[TD([[makeQuery(id+"F25.imprint","IMPRINT",EDGE,{"derivedFrom":sQuery(id+"F25.wireOp",EDGE,"E139.bottom")}),-1.0]])]});
            var Q3;
            Q3=makeQuery(id+"F25.imprint","IMPRINT",FACE,{"disambiguationData":[TD([[makeQuery(id+"F25.imprint","IMPRINT",EDGE,{"derivedFrom":sQuery(id+"F25.wireOp",EDGE,"E140.bottom")}),-1.0]])]});
            var Q4;
            Q4=makeQuery(id+"F25.imprint","IMPRINT",FACE,{"disambiguationData":[TD([[makeQuery(id+"F25.imprint","IMPRINT",EDGE,{"derivedFrom":sQuery(id+"F25.wireOp",EDGE,"E141.bottom")}),-1.0]])]});
            extrude(context, id + "F26", {"entities" : qUnion([Q0, Q1, Q2, Q3, Q4]), "operationType" : NewBodyOperationType.REMOVE, "oppositeDirection" : true, "depth" : 10 * mm, "offsetDistance" : 25 * mm});
        }
        {
            var Q0;
            Q0=makeQuery(id+"F1.opExtrude","SWEPT_FACE",FACE,{"disambiguationData":[OSD([sQuery(id+"F0.wireOp",EDGE,"E61")])]});
            var sketch = newSketch(context, id + "F27", { "sketchPlane" : qUnion([Q0])});
            skLineSegment(sketch, "E143.bottom", {"start": v(1676.7, 200) * mm, "end": v(2376.7, 200) * mm});
            skLineSegment(sketch, "E143.top", {"start": v(1676.7, 800) * mm, "end": v(2376.7, 800) * mm});
            skLineSegment(sketch, "E143.left", {"start": v(1676.7, 200) * mm, "end": v(1676.7, 800) * mm});
            skLineSegment(sketch, "E143.right", {"start": v(2376.7, 200) * mm, "end": v(2376.7, 800) * mm});
            skSolve(sketch);
        }
        {
            var Q0;
            Q0=makeQuery(id+"F27.imprint","IMPRINT",FACE,{"disambiguationData":[TD([[makeQuery(id+"F27.imprint","IMPRINT",EDGE,{"derivedFrom":sQuery(id+"F27.wireOp",EDGE,"E143.bottom")}),1.0]])]});
            extrude(context, id + "F28", {"entities" : qUnion([Q0]), "depth" : 60 * mm, "offsetDistance" : 25 * mm});
        }
        {
            var Q0;
            {var subQ5=sQuery(id+"F0.wireOp",EDGE,"E93");Q0=makeQuery(id+"F0.imprint","IMPRINT",FACE,{"disambiguationData":[TD([[makeQuery(id+"F0.imprint","IMPRINT",EDGE,{"derivedFrom":subQ5}),-1.0]])]});}
            var Q1;
            {var subQ0=sQuery(id+"F0.wireOp",EDGE,"E94");Q1=makeQuery(id+"F0.imprint","IMPRINT",FACE,{"disambiguationData":[TD([[makeQuery(id+"F0.imprint","IMPRINT",EDGE,{"derivedFrom":subQ0}),1.0]])]});}
            extrude(context, id + "F29", {"entities" : qUnion([Q0, Q1]), "depth" : 2400 * mm, "offsetDistance" : 25 * mm});
        }
        {
            var Q0;
            Q0=makeQuery(id+"F0.imprint","IMPRINT",FACE,{"disambiguationData":[TD([[makeQuery(id+"F0.imprint","IMPRINT",EDGE,{"derivedFrom":sQuery(id+"F0.wireOp",EDGE,"E99")}),1.0]])]});
            extrude(context, id + "F30", {"entities" : qUnion([Q0]), "depth" : 1000 * mm, "offsetDistance" : 25 * mm});
        }
    });
